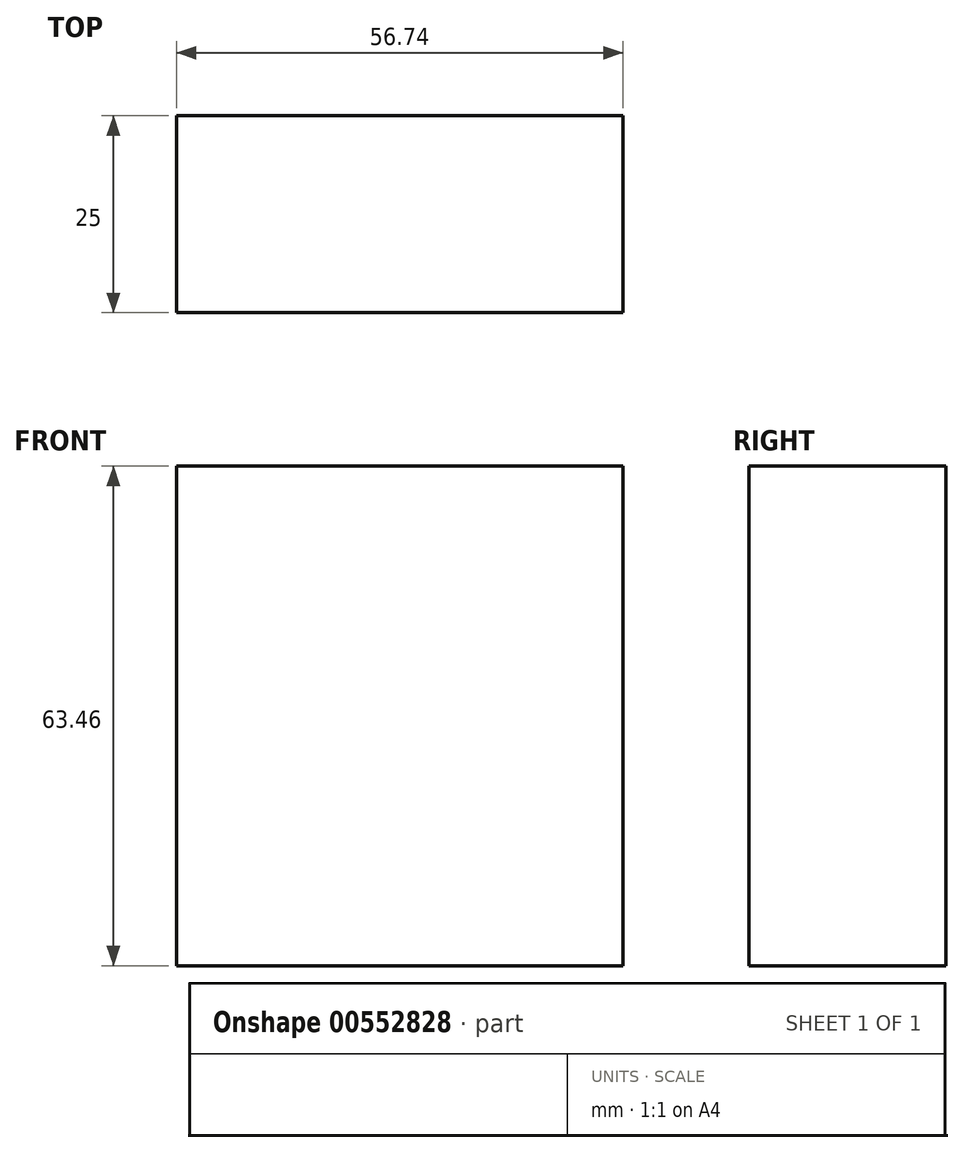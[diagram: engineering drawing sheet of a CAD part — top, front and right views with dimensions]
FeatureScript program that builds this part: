
annotation { "Feature Type Name" : "Feature", "Feature Type Description" : "" }
export const myFeature = defineFeature(function(context is Context, id is Id, definition is map)
    precondition{}
    {
        {
            var Q0;
            Q0=qCreatedBy(makeId("Front.planeOp"),FACE);
            var sketch = newSketch(context, id + "F0", { "sketchPlane" : qUnion([Q0])});
            skLineSegment(sketch, "E0.bottom", {"start": v(-134.87, 60.58) * mm, "end": v(-78.13, 60.58) * mm});
            skLineSegment(sketch, "E0.top", {"start": v(-134.87, -2.88) * mm, "end": v(-78.13, -2.88) * mm});
            skLineSegment(sketch, "E0.left", {"start": v(-134.87, 60.58) * mm, "end": v(-134.87, -2.88) * mm});
            skLineSegment(sketch, "E0.right", {"start": v(-78.13, 60.58) * mm, "end": v(-78.13, -2.88) * mm});
            skSolve(sketch);
        }
        {
            var Q0;
            Q0 = qSketchRegion(id + "F0", true);
            extrude(context, id + "F1", {"entities" : qUnion([Q0]), "depth" : 25 * mm, "offsetDistance" : 25 * mm});
        }
    });
